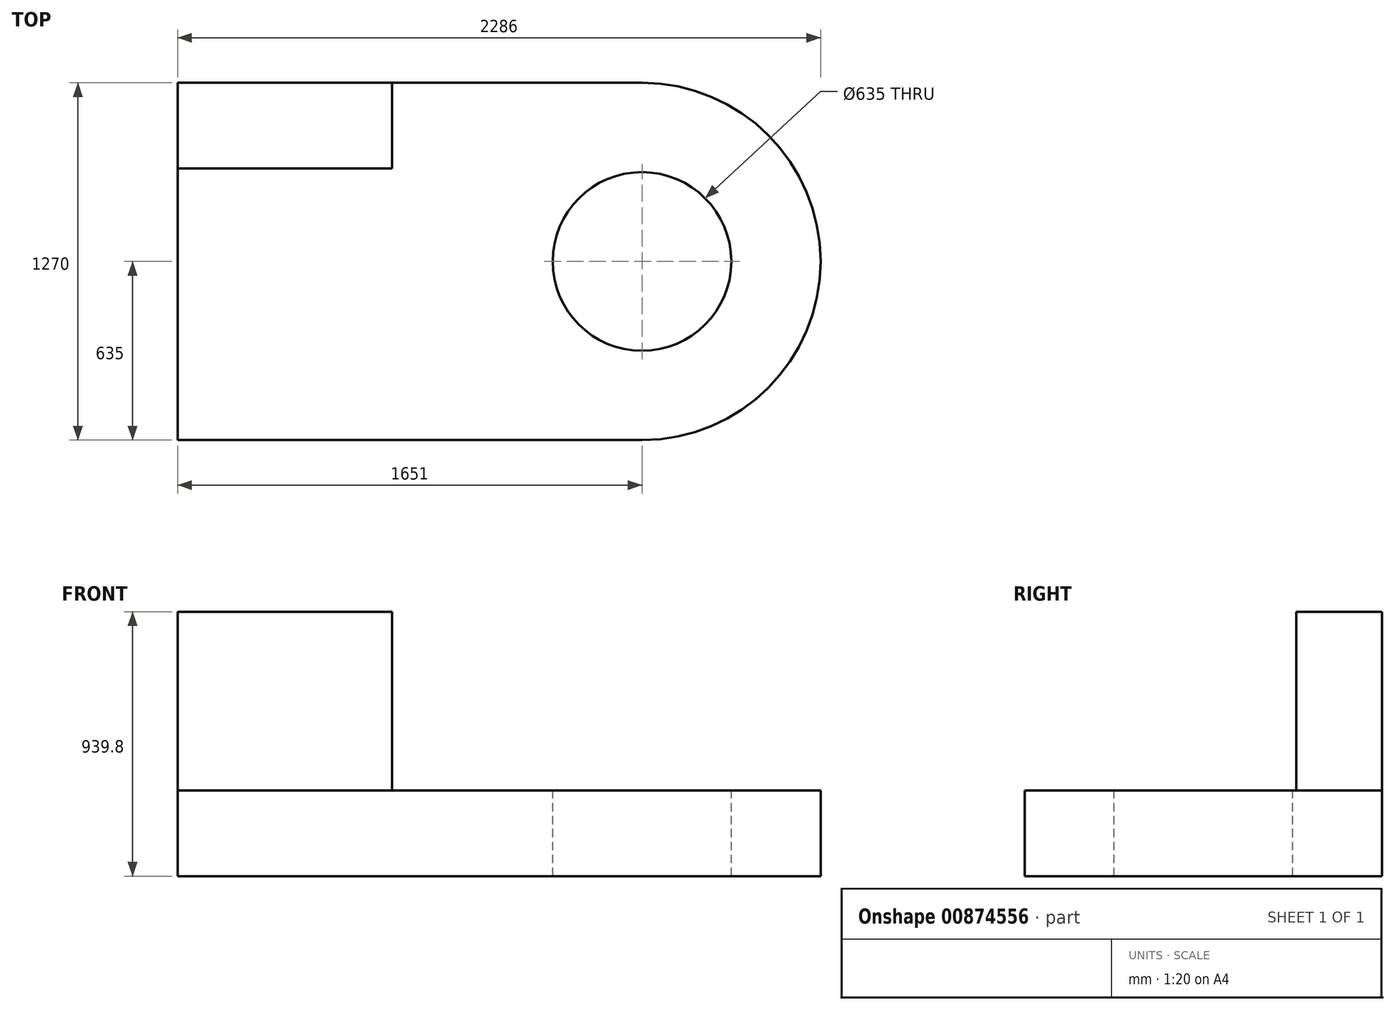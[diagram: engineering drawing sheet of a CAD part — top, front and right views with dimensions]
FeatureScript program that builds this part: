
annotation { "Feature Type Name" : "Feature", "Feature Type Description" : "" }
export const myFeature = defineFeature(function(context is Context, id is Id, definition is map)
    precondition{}
    {
        {
            var Q0;
            Q0=qCreatedBy(makeId("Front.planeOp"),FACE);
            var sketch = newSketch(context, id + "F0", { "sketchPlane" : qUnion([Q0])});
            skLineSegment(sketch, "E0.bottom", {"start": v(0, 0) * mm, "end": v(-762, 0) * mm});
            skLineSegment(sketch, "E0.top", {"start": v(0, 939.8) * mm, "end": v(-762, 939.8) * mm});
            skLineSegment(sketch, "E0.left", {"start": v(0, 0) * mm, "end": v(0, 939.8) * mm});
            skLineSegment(sketch, "E0.right", {"start": v(-762, 0) * mm, "end": v(-762, 939.8) * mm});
            skSolve(sketch);
        }
        {
            var Q0;
            Q0=makeQuery(id+"F0.imprint","IMPRINT",FACE,{"disambiguationData":[TD([[makeQuery(id+"F0.imprint","IMPRINT",EDGE,{"derivedFrom":sQuery(id+"F0.wireOp",EDGE,"E0.bottom")}),-1.0]])]});
            extrude(context, id + "F1", {"entities" : qUnion([Q0]), "depth" : 304.8 * mm, "offsetDistance" : 25.4 * mm});
        }
        {
            var Q0;
            Q0=makeQuery(id+"F1.opExtrude","CAP_FACE",FACE,{"disambiguationData":[OSD([sQuery(id+"F0.wireOp",EDGE,"E0.bottom"),sQuery(id+"F0.wireOp",EDGE,"E0.top"),sQuery(id+"F0.wireOp",EDGE,"E0.left"),sQuery(id+"F0.wireOp",EDGE,"E0.right")])],"isStart":false});
            var sketch = newSketch(context, id + "F2", { "sketchPlane" : qUnion([Q0])});
            skLineSegment(sketch, "E1.bottom", {"start": v(0, 0) * mm, "end": v(-762, 0) * mm});
            skLineSegment(sketch, "E1.top", {"start": v(0, 304.8) * mm, "end": v(-762, 304.8) * mm});
            skLineSegment(sketch, "E1.left", {"start": v(0, 0) * mm, "end": v(0, 304.8) * mm});
            skLineSegment(sketch, "E1.right", {"start": v(-762, 0) * mm, "end": v(-762, 304.8) * mm});
            skSolve(sketch);
        }
        {
            var Q0;
            Q0=makeQuery(id+"F2.imprint","IMPRINT",FACE,{"disambiguationData":[TD([[makeQuery(id+"F2.imprint","IMPRINT",EDGE,{"derivedFrom":sQuery(id+"F2.wireOp",EDGE,"E1.bottom")}),-1.0]])]});
            extrude(context, id + "F3", {"entities" : qUnion([Q0]), "operationType" : NewBodyOperationType.ADD, "depth" : 965.2 * mm, "offsetDistance" : 25.4 * mm});
        }
        {
            var Q0;
            Q0=makeQuery(id+"F3.boolean.opBoolean","MERGE",FACE,{"derivedFrom":[makeQuery(id+"F1.opExtrude","SWEPT_FACE",FACE,{"disambiguationData":[OSD([sQuery(id+"F0.wireOp",EDGE,"E0.left")])]}),makeQuery(id+"F3.opExtrude","SWEPT_FACE",FACE,{"disambiguationData":[OSD([sQuery(id+"F2.wireOp",EDGE,"E1.left")])]})]});
            var sketch = newSketch(context, id + "F4", { "sketchPlane" : qUnion([Q0])});
            skLineSegment(sketch, "E2", {"start": v(-304.8, 304.8) * mm, "end": v(0, 304.8) * mm});
            skSolve(sketch);
        }
        {
            var Q0;
            {var subQ3=sQuery(id+"F4.wireOp",EDGE,"E2");Q0=makeQuery(id+"F4.imprint","IMPRINT",FACE,{"disambiguationData":[TD([[makeQuery(id+"F4.imprint","IMPRINT",EDGE,{"derivedFrom":subQ3}),-1.0]])]});}
            extrude(context, id + "F5", {"entities" : qUnion([Q0]), "operationType" : NewBodyOperationType.ADD, "depth" : 889 * mm, "offsetDistance" : 25.4 * mm});
        }
        {
            var Q0;
            {var subQ0=sQuery(id+"F2.wireOp",EDGE,"E1.top");Q0=makeQuery(id+"F5.boolean.opBoolean","MERGE",FACE,{"derivedFrom":[makeQuery(id+"F3.opExtrude","SWEPT_FACE",FACE,{"disambiguationData":[OSD([subQ0])]}),makeQuery(id+"F5.opExtrude","SWEPT_FACE",FACE,{"disambiguationData":[OSD([sQuery(id+"F0.wireOp",EDGE,"E0.left"),subQ0,sQuery(id+"F2.wireOp",EDGE,"E1.left"),sQuery(id+"F4.wireOp",EDGE,"E2")])]})]});}
            var sketch = newSketch(context, id + "F6", { "sketchPlane" : qUnion([Q0])});
            skCircle(sketch, "E3", {"center": v(889, -635) * mm, "radius": 635 * mm});
            skSolve(sketch);
        }
        {
            var Q0;
            {var subQ1=sQuery(id+"F2.wireOp",EDGE,"E1.left");var subQ2=sQuery(id+"F2.wireOp",EDGE,"E1.top");var subQ3=sQuery(id+"F0.wireOp",EDGE,"E0.left");var subQ4=sQuery(id+"F4.wireOp",EDGE,"E2");var subQ5=makeQuery(id+"F5.opExtrude","CAP_EDGE",EDGE,{"disambiguationData":[OSD([subQ3,subQ2,subQ1,subQ4])],"isStart":false});Q0=makeQuery(id+"F6.imprint","IMPRINT",FACE,{"disambiguationData":[TD([[makeQuery(id+"F6.imprint","IMPRINT",EDGE,{"derivedFrom":subQ5}),-1.0]])]});}
            extrude(context, id + "F7", {"entities" : qUnion([Q0]), "operationType" : NewBodyOperationType.ADD, "oppositeDirection" : true, "depth" : 304.8 * mm, "offsetDistance" : 25.4 * mm});
        }
        {
            var Q0;
            {var subQ0=sQuery(id+"F4.wireOp",EDGE,"E2");var subQ1=sQuery(id+"F2.wireOp",EDGE,"E1.left");var subQ2=sQuery(id+"F2.wireOp",EDGE,"E1.top");var subQ3=sQuery(id+"F0.wireOp",EDGE,"E0.left");Q0=makeQuery(id+"F7.boolean.opBoolean","MERGE",FACE,{"derivedFrom":[makeQuery(id+"F5.boolean.opBoolean","MERGE",FACE,{"derivedFrom":[makeQuery(id+"F3.opExtrude","SWEPT_FACE",FACE,{"disambiguationData":[OSD([subQ2])]}),makeQuery(id+"F5.opExtrude","SWEPT_FACE",FACE,{"disambiguationData":[OSD([subQ3,subQ2,subQ1,subQ0])]})]}),makeQuery(id+"F7.opExtrude","CAP_FACE",FACE,{"disambiguationData":[OSD([subQ3,subQ2,subQ1,subQ0,sQuery(id+"F6.wireOp",EDGE,"E3")])],"isStart":true})]});}
            var sketch = newSketch(context, id + "F8", { "sketchPlane" : qUnion([Q0])});
            skCircle(sketch, "E4", {"center": v(889, -635) * mm, "radius": 317.5 * mm});
            skSolve(sketch);
        }
        {
            var Q0;
            Q0=makeQuery(id+"F8.imprint","IMPRINT",FACE,{"disambiguationData":[TD([[makeQuery(id+"F8.imprint","IMPRINT",EDGE,{"derivedFrom":sQuery(id+"F8.wireOp",EDGE,"E4")}),1.0]])]});
            extrude(context, id + "F9", {"entities" : qUnion([Q0]), "operationType" : NewBodyOperationType.REMOVE, "oppositeDirection" : true, "depth" : 2514.6 * mm, "offsetDistance" : 25.4 * mm});
        }
    });
